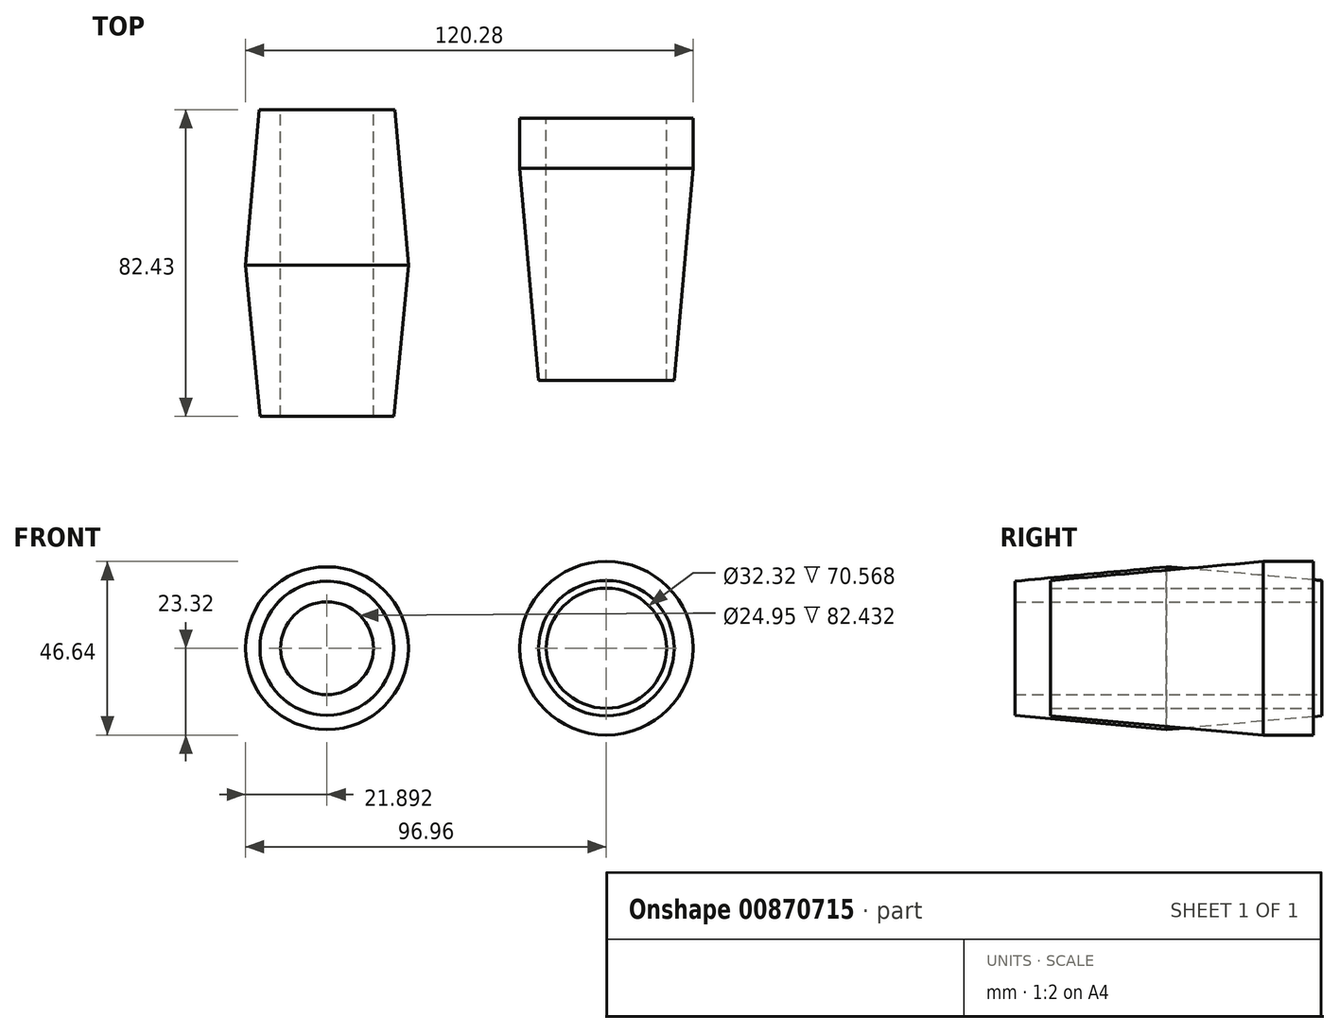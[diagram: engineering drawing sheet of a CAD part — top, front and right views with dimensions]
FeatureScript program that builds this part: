
annotation { "Feature Type Name" : "Feature", "Feature Type Description" : "" }
export const myFeature = defineFeature(function(context is Context, id is Id, definition is map)
    precondition{}
    {
        {
            var Q0;
            Q0=qCreatedBy(makeId("Top.planeOp"),FACE);
            var sketch = newSketch(context, id + "F0", { "sketchPlane" : qUnion([Q0])});
            skLineSegment(sketch, "E0", {"start": v(-40.4, 64.74) * mm, "end": v(-40.4, -35.49) * mm});
            skLineSegment(sketch, "E1", {"start": v(-27.92, 64.74) * mm, "end": v(-27.92, 22.4) * mm});
            skLineSegment(sketch, "E2", {"start": v(-27.92, -17.7) * mm, "end": v(-27.92, 22.4) * mm});
            skLineSegment(sketch, "E3", {"start": v(-27.92, -17.7) * mm, "end": v(-22.4, -17.7) * mm});
            skLineSegment(sketch, "E4", {"start": v(-22.4, -17.7) * mm, "end": v(-18.5, 23.01) * mm});
            skLineSegment(sketch, "E5", {"start": v(-18.5, 23.01) * mm, "end": v(-22.19, 64.74) * mm});
            skLineSegment(sketch, "E6", {"start": v(-22.19, 64.74) * mm, "end": v(-27.92, 64.74) * mm});
            skSolve(sketch);
        }
        {
            var Q0;
            Q0=makeQuery(id+"F0.imprint","IMPRINT",FACE,{"disambiguationData":[TD([[makeQuery(id+"F0.imprint","IMPRINT",EDGE,{"derivedFrom":sQuery(id+"F0.wireOp",EDGE,"E1")}),1.0]])]});
            var Q1;
            Q1=sQuery(id+"F0.wireOp",EDGE,"E0");
            revolve(context, id + "F1", {"surfaceOperationType" : NewSurfaceOperationType.NEW, "entities" : qUnion([Q0]), "axis" : qUnion([Q1]), "revolveType" : RevolveType.FULL});
        }
        {
            var Q0;
            Q0=qCreatedBy(makeId("Top.planeOp"),FACE);
            var sketch = newSketch(context, id + "F2", { "sketchPlane" : qUnion([Q0])});
            skLineSegment(sketch, "E7", {"start": v(34.67, 62.9) * mm, "end": v(34.67, -8.08) * mm});
            skLineSegment(sketch, "E8", {"start": v(50.83, 62.49) * mm, "end": v(50.83, -8.08) * mm});
            skLineSegment(sketch, "E9", {"start": v(50.83, -8.08) * mm, "end": v(52.88, -8.08) * mm});
            skLineSegment(sketch, "E10", {"start": v(52.88, -8.08) * mm, "end": v(58, 48.99) * mm});
            skLineSegment(sketch, "E11", {"start": v(58, 48.99) * mm, "end": v(58, 62.49) * mm});
            skLineSegment(sketch, "E12", {"start": v(58, 62.49) * mm, "end": v(50.83, 62.49) * mm});
            skSolve(sketch);
        }
        {
            var Q0;
            Q0=makeQuery(id+"F2.imprint","IMPRINT",FACE,{"disambiguationData":[TD([[makeQuery(id+"F2.imprint","IMPRINT",EDGE,{"derivedFrom":sQuery(id+"F2.wireOp",EDGE,"E8")}),1.0]])]});
            var Q1;
            Q1=sQuery(id+"F2.wireOp",EDGE,"E7");
            revolve(context, id + "F3", {"surfaceOperationType" : NewSurfaceOperationType.NEW, "entities" : qUnion([Q0]), "axis" : qUnion([Q1]), "revolveType" : RevolveType.FULL});
        }
    });
